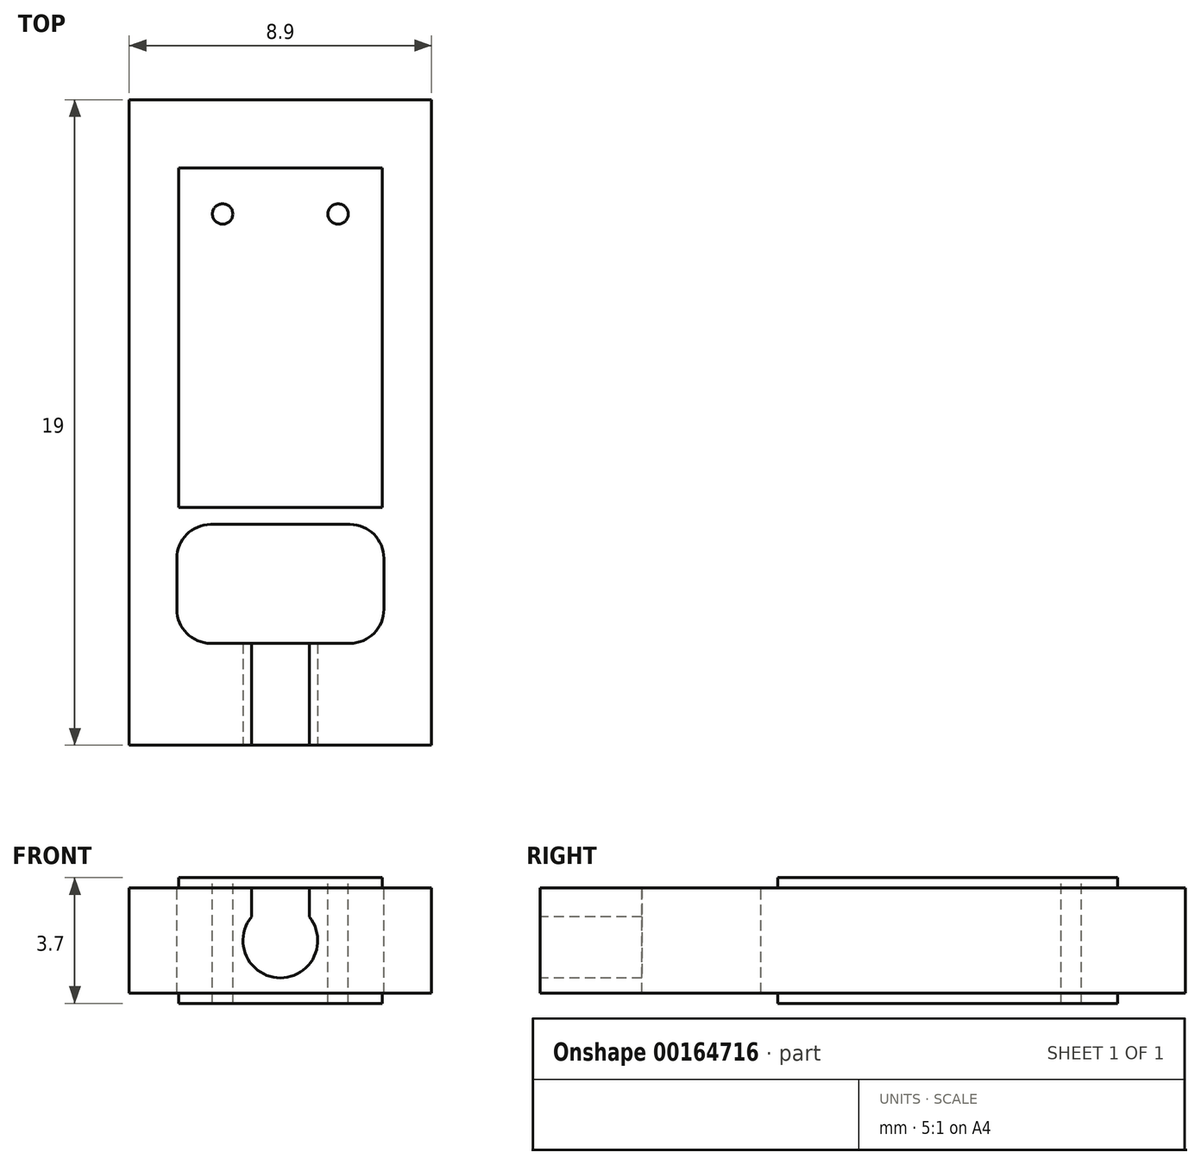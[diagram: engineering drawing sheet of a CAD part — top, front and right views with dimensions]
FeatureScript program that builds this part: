
annotation { "Feature Type Name" : "Feature", "Feature Type Description" : "" }
export const myFeature = defineFeature(function(context is Context, id is Id, definition is map)
    precondition{}
    {
        {
            assignVariable(context, id + "F0", {"name" : "Main_Width", "anyValue" : 8.9});
        }
        {
            assignVariable(context, id + "F1", {"name" : "Thickness1", "anyValue" : 3.1});
        }
        {
            assignVariable(context, id + "F2", {"name" : "Thickness2", "anyValue" : 3.7});
        }
        {
            var Q0;
            Q0=qCreatedBy(makeId("Right.planeOp"),FACE);
            var sketch = newSketch(context, id + "F3", { "sketchPlane" : qUnion([Q0])});
            skLineSegment(sketch, "E0", {"start": v(0, 0) * mm, "end": v(0, 1.55) * mm});
            skLineSegment(sketch, "E1", {"start": v(0, 1.55) * mm, "end": v(19, 1.55) * mm});
            skLineSegment(sketch, "E2", {"start": v(19, 1.55) * mm, "end": v(19, 0) * mm});
            skLineSegment(sketch, "E3", {"start": v(0, 0) * mm, "end": v(19, 0) * mm, "construction": true});
            skLineSegment(sketch, "E4.MirrorCS", {"start": v(0, -1.55) * mm, "end": v(19, -1.55) * mm});
            skLineSegment(sketch, "E5.MirrorCS", {"start": v(0, 0) * mm, "end": v(0, -1.55) * mm});
            skLineSegment(sketch, "E6.MirrorCS", {"start": v(19, -1.55) * mm, "end": v(19, 0) * mm});
            skSolve(sketch);
        }
        {
            var Q0;
            Q0=makeQuery(id+"F3.imprint","IMPRINT",FACE,{"disambiguationData":[TD([[makeQuery(id+"F3.imprint","IMPRINT",EDGE,{"derivedFrom":sQuery(id+"F3.wireOp",EDGE,"E0")}),-1.0]])]});
            extrude(context, id + "F4", {"entities" : qUnion([Q0]), "depth" : (getVariable(context, 'Main_Width')) * mm});
        }
        {
            var Q0;
            Q0=makeQuery(id+"F4.opExtrude","SWEPT_FACE",FACE,{"disambiguationData":[OSD([sQuery(id+"F3.wireOp",EDGE,"E1")])]});
            cPlane(context, id + "F5", {"entities" : qUnion([Q0]), "cplaneType" : CPlaneType.OFFSET, "offset" : ((getVariable(context, 'Thickness2') - getVariable(context, 'Thickness1')) / 2) * mm, "width" : 150 * mm, "height" : 150 * mm});
        }
        {
            var Q0;
            Q0=qCreatedBy(id+"F5.planeOp",FACE);
            var sketch = newSketch(context, id + "F6", { "sketchPlane" : qUnion([Q0])});
            skLineSegment(sketch, "E7.bottom", {"start": v(1.45, 17) * mm, "end": v(7.45, 17) * mm});
            skLineSegment(sketch, "E7.top", {"start": v(1.45, 7) * mm, "end": v(7.45, 7) * mm});
            skLineSegment(sketch, "E7.left", {"start": v(1.45, 17) * mm, "end": v(1.45, 7) * mm});
            skLineSegment(sketch, "E7.right", {"start": v(7.45, 17) * mm, "end": v(7.45, 7) * mm});
            skPoint(sketch, "E7.middle", {"position": v(4.45, 12) * mm});
            skLineSegment(sketch, "E8.0", {"start": v(8.9, 19) * mm, "end": v(0, 19) * mm});
            skLineSegment(sketch, "E9.0", {"start": v(0, 0) * mm, "end": v(0, 19) * mm});
            skPoint(sketch, "E10", {"position": v(4.45, 19) * mm});
            skPoint(sketch, "E11", {"position": v(0, 9.5) * mm});
            skSolve(sketch);
        }
        {
            var Q0;
            Q0=makeQuery(id+"F6.imprint","IMPRINT",FACE,{"disambiguationData":[TD([[makeQuery(id+"F6.imprint","IMPRINT",EDGE,{"derivedFrom":sQuery(id+"F6.wireOp",EDGE,"E7.bottom")}),-1.0]])]});
            extrude(context, id + "F7", {"entities" : qUnion([Q0]), "operationType" : NewBodyOperationType.ADD, "oppositeDirection" : true, "depth" : (getVariable(context, 'Thickness2')) * mm});
        }
        {
            var Q0;
            Q0=qCreatedBy(id+"F5.planeOp",FACE);
            var sketch = newSketch(context, id + "F8", { "sketchPlane" : qUnion([Q0])});
            skLineSegment(sketch, "E12.0", {"start": v(8.9, 0) * mm, "end": v(0, 0) * mm});
            skLineSegment(sketch, "E13", {"start": v(4.45, 15.64) * mm, "end": v(4.45, 0) * mm, "construction": true});
            skPoint(sketch, "E13.endSnap0", {"position": v(4.45, 0) * mm});
            skLineSegment(sketch, "E14.bottom", {"start": v(2.4, 3) * mm, "end": v(6.5, 3) * mm});
            skLineSegment(sketch, "E14.top", {"start": v(2.4, 6.5) * mm, "end": v(6.5, 6.5) * mm});
            skLineSegment(sketch, "E14.left", {"start": v(2.4, 3) * mm, "end": v(2.4, 6.5) * mm, "construction": true});
            skLineSegment(sketch, "E14.right", {"start": v(6.5, 3) * mm, "end": v(6.5, 6.5) * mm, "construction": true});
            skPoint(sketch, "E14.middle", {"position": v(4.45, 4.75) * mm});
            skArc(sketch, "E15", {"start": v(1.4, 4) * mm, "mid": v(1.7, 3.3) * mm, "end": v(2.4, 3) * mm});
            skArc(sketch, "E16", {"start": v(2.4, 6.5) * mm, "mid": v(1.7, 6.2) * mm, "end": v(1.4, 5.5) * mm});
            skLineSegment(sketch, "E17", {"start": v(1.4, 4) * mm, "end": v(1.4, 5.5) * mm});
            skArc(sketch, "E18.MirrorCS", {"start": v(6.5, 6.5) * mm, "mid": v(7.2, 6.2) * mm, "end": v(7.5, 5.5) * mm});
            skLineSegment(sketch, "E19.MirrorCS", {"start": v(7.5, 4) * mm, "end": v(7.5, 5.5) * mm});
            skArc(sketch, "E20.MirrorCS", {"start": v(7.5, 4) * mm, "mid": v(7.2, 3.3) * mm, "end": v(6.5, 3) * mm});
            skCircle(sketch, "E21", {"center": v(2.75, 15.64) * mm, "radius": 0.3 * mm});
            skCircle(sketch, "E22", {"center": v(6.15, 15.64) * mm, "radius": 0.3 * mm});
            skSolve(sketch);
        }
        {
            var Q0;
            Q0=makeQuery(id+"F8.imprint","IMPRINT",FACE,{"disambiguationData":[TD([[makeQuery(id+"F8.imprint","IMPRINT",EDGE,{"derivedFrom":sQuery(id+"F8.wireOp",EDGE,"E14.bottom")}),1.0]])]});
            var Q1;
            Q1=makeQuery(id+"F8.imprint","IMPRINT",FACE,{"disambiguationData":[TD([[makeQuery(id+"F8.imprint","IMPRINT",EDGE,{"derivedFrom":sQuery(id+"F8.wireOp",EDGE,"E21")}),1.0]])]});
            var Q2;
            Q2=makeQuery(id+"F8.imprint","IMPRINT",FACE,{"disambiguationData":[TD([[makeQuery(id+"F8.imprint","IMPRINT",EDGE,{"derivedFrom":sQuery(id+"F8.wireOp",EDGE,"E22")}),1.0]])]});
            extrude(context, id + "F9", {"entities" : qUnion([Q0, Q1, Q2]), "operationType" : NewBodyOperationType.REMOVE, "endBound" : BoundingType.THROUGH_ALL, "oppositeDirection" : true, "depth" : 25 * mm});
        }
        {
            var Q0;
            Q0=makeQuery(id+"F4.opExtrude","SWEPT_FACE",FACE,{"disambiguationData":[OSD([sQuery(id+"F3.wireOp",EDGE,"E0"),sQuery(id+"F3.wireOp",EDGE,"E5.MirrorCS")])]});
            var sketch = newSketch(context, id + "F10", { "sketchPlane" : qUnion([Q0])});
            skLineSegment(sketch, "E23.0.0", {"start": v(0, 1.55) * mm, "end": v(0, -1.55) * mm});
            skLineSegment(sketch, "E23.0.1", {"start": v(0, -1.55) * mm, "end": v(8.9, -1.55) * mm});
            skLineSegment(sketch, "E23.0.2", {"start": v(8.9, -1.55) * mm, "end": v(8.9, 1.55) * mm});
            skLineSegment(sketch, "E23.0.3", {"start": v(8.9, 1.55) * mm, "end": v(0, 1.55) * mm});
            skArc(sketch, "E24", {"start": v(3.6, 0.7) * mm, "mid": v(4.45, -1.1) * mm, "end": v(5.3, 0.7) * mm});
            skLineSegment(sketch, "E25", {"start": v(4.45, 1.55) * mm, "end": v(4.45, -1.55) * mm, "construction": true});
            skLineSegment(sketch, "E26", {"start": v(3.6, 0.7) * mm, "end": v(3.6, 1.55) * mm});
            skLineSegment(sketch, "E27", {"start": v(5.3, 0.7) * mm, "end": v(5.3, 1.55) * mm});
            skSolve(sketch);
        }
        {
            var Q0;
            Q0=makeQuery(id+"F10.imprint","IMPRINT",FACE,{"disambiguationData":[TD([[makeQuery(id+"F10.imprint","IMPRINT",EDGE,{"derivedFrom":sQuery(id+"F10.wireOp",EDGE,"E24")}),1.0]])]});
            extrude(context, id + "F11", {"entities" : qUnion([Q0]), "operationType" : NewBodyOperationType.REMOVE, "endBound" : BoundingType.UP_TO_NEXT, "oppositeDirection" : true, "depth" : 25 * mm});
        }
    });
